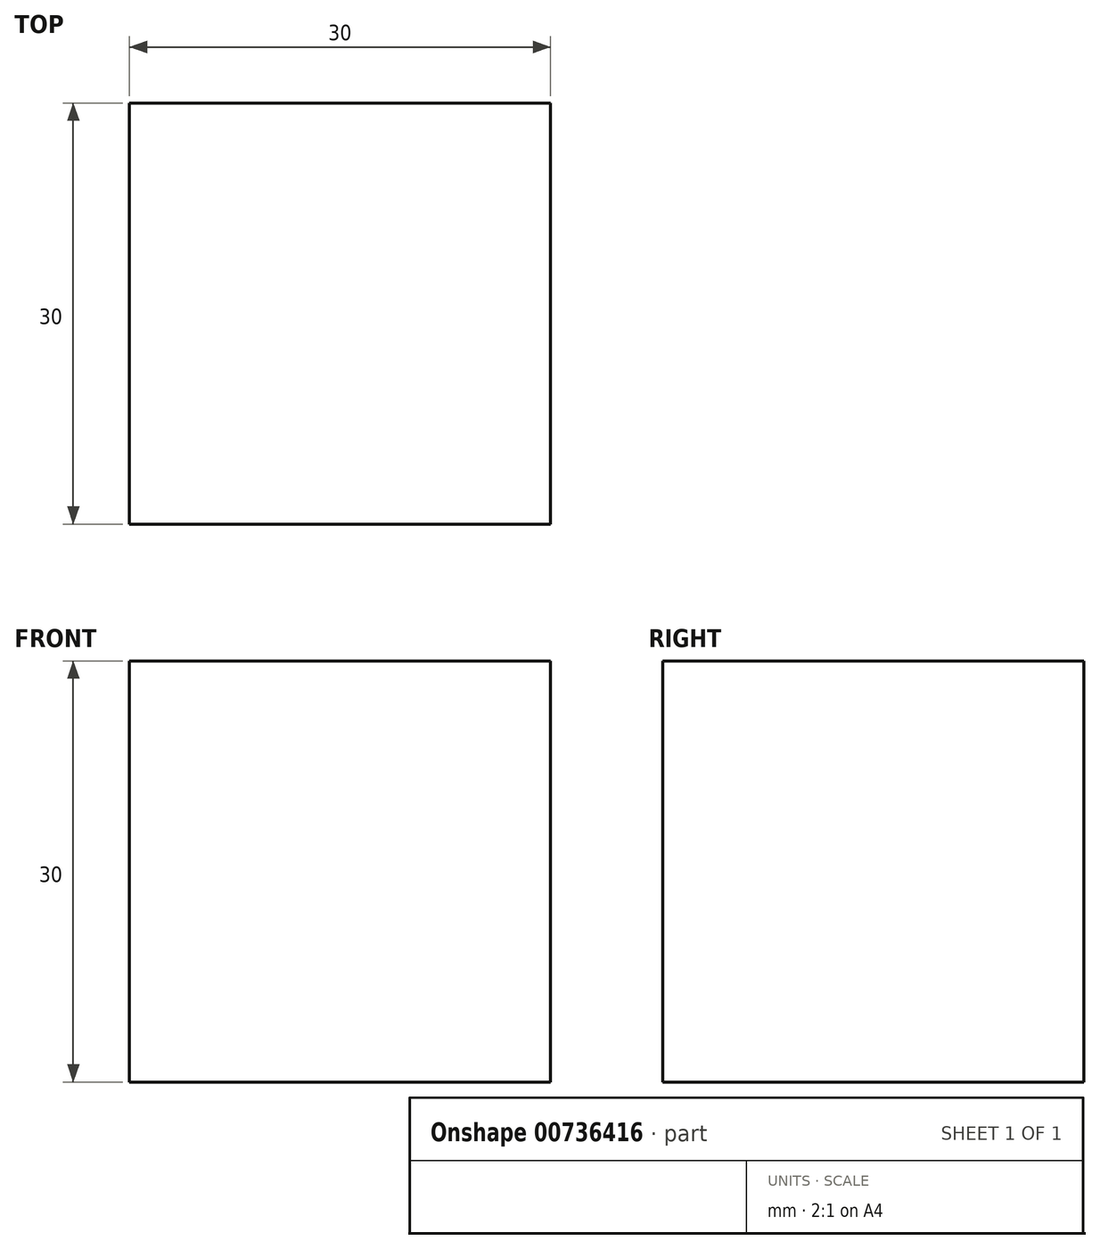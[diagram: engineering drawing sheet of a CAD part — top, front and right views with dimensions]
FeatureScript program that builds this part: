
annotation { "Feature Type Name" : "Feature", "Feature Type Description" : "" }
export const myFeature = defineFeature(function(context is Context, id is Id, definition is map)
    precondition{}
    {
        {
            var Q0;
            Q0=qCreatedBy(makeId("Top.planeOp"),FACE);
            var sketch = newSketch(context, id + "F0", { "sketchPlane" : qUnion([Q0])});
            skLineSegment(sketch, "E0.bottom", {"start": v(-15, -15) * mm, "end": v(15, -15) * mm});
            skLineSegment(sketch, "E0.top", {"start": v(-15, 15) * mm, "end": v(15, 15) * mm});
            skLineSegment(sketch, "E0.left", {"start": v(-15, -15) * mm, "end": v(-15, 15) * mm});
            skLineSegment(sketch, "E0.right", {"start": v(15, -15) * mm, "end": v(15, 15) * mm});
            skSolve(sketch);
        }
        {
            var Q0;
            Q0=makeQuery(id+"F0.imprint","IMPRINT",FACE,{"disambiguationData":[TD([[makeQuery(id+"F0.imprint","IMPRINT",EDGE,{"derivedFrom":sQuery(id+"F0.wireOp",EDGE,"E0.bottom")}),1.0]])]});
            extrude(context, id + "F1", {"entities" : qUnion([Q0]), "depth" : 30 * mm, "offsetDistance" : 25 * mm});
        }
    });
